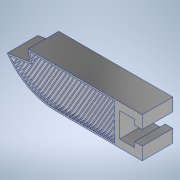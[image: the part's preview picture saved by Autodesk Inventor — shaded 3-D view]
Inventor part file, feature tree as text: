
AUTODESK INVENTOR PART (.ipt)
format: ipt  version: 2022 (Build 260153000, 153)  size: 600,576 bytes
history: native  units: mm
features: extrude x7, sketch x6, fillet x1, shell x1, projected_geometry x1
ambient origin geometry x8: Origin, YZ Plane, XZ Plane, XY Plane, X Axis, Y Axis, Z Axis, Center Point
bodies: Body1 (feature_tree)
feature tree (16):
  extrude  "Extrusion2"  Depth=5.8mm
  extrude  "Extrusion5"  Depth=12.0mm TaperAngle=0.0deg
  fillet  "Fillet2"  Radius=45.0mm
  shell  "Shell1"  Thickness=15.6mm
  extrude  "Extrusion7"  TaperAngle=0.0deg  [1 undecoded]
  extrude  "Extrusion8"  Depth=9.6mm
  extrude  "Extrusion9"  Depth=9.0mm
  extrude  "Extrusion10"  Depth=23.0mm
  extrude  "Extrusion11"  Depth=0.62mm
  sketch  "Sketch8"  dims[d41=5.8mm d48=44.0mm]
  sketch  "Sketch13"  dims[d50=3.0mm d56=12.0mm d57=0.0mm d63=45.0mm d67=15.6mm d71=0.0mm]
  sketch  "Sketch14"  dims[d80=17.453293mm d82=0.0mm d83=0.0mm]
  projected_geometry  "Projected Loop1"
  sketch  "Sketch15"  dims[d87=5.6mm d88=9.6mm]
  sketch  "Sketch16"  dims[d95=4.0mm d96=9.0mm]
  sketch  "Sketch17"  dims[d97=15.6mm d98=23.0mm d99=0.62mm d100=12.0mm d101=0.0mm d102=10.747401mm d103=12.0mm d104=0.0mm d105=0.38mm d107=0.38mm d1=0.38mm d110=0.38mm d111=0.38mm d112=0.38mm d113=0.38mm d127=12.0mm d128=0.0mm d129=0.38mm d131=0.38mm d132=0.38mm d133=0.38mm d134=0.38mm d135=0.38mm d136=0.38mm d137=0.38mm d138=0.38mm d139=0.38mm d151=0.38mm d157=0.38mm d161=0.38mm d163=0.38mm d168=0.89mm d169=0.38mm d170=0.89mm d171=0.89mm d172=0.38mm d173=0.89mm d174=0.89mm d175=0.38mm d176=0.89mm d178=0.38mm d179=0.89mm d182=0.89mm d184=0.89mm d185=120.0deg d186=120.0deg d187=120.0deg d189=0.89mm d193=0.89mm d194=0.89mm d195=0.89mm d196=0.89mm d197=0.89mm d200=0.38mm d201=120.0deg d202=0.89mm d205=0.89mm d206=0.89mm d207=0.89mm d209=0.89mm d210=0.38mm d211=0.38mm d213=0.89mm d214=0.38mm d215=0.38mm d216=0.38mm d217=0.89mm d218=0.89mm d219=12.0mm d220=0.0mm d221=0.89mm d222=0.89mm d223=0.89mm d224=0.38mm d225=0.89mm d226=0.89mm d227=0.89mm d228=0.89mm d229=0.89mm d230=12.0mm d231=0.0mm]
note: 1 required parameter value undecoded (feature->parameter linkage not recoverable at this tier; creation-order binding heuristic only, values carry confidence <= 0.55)
